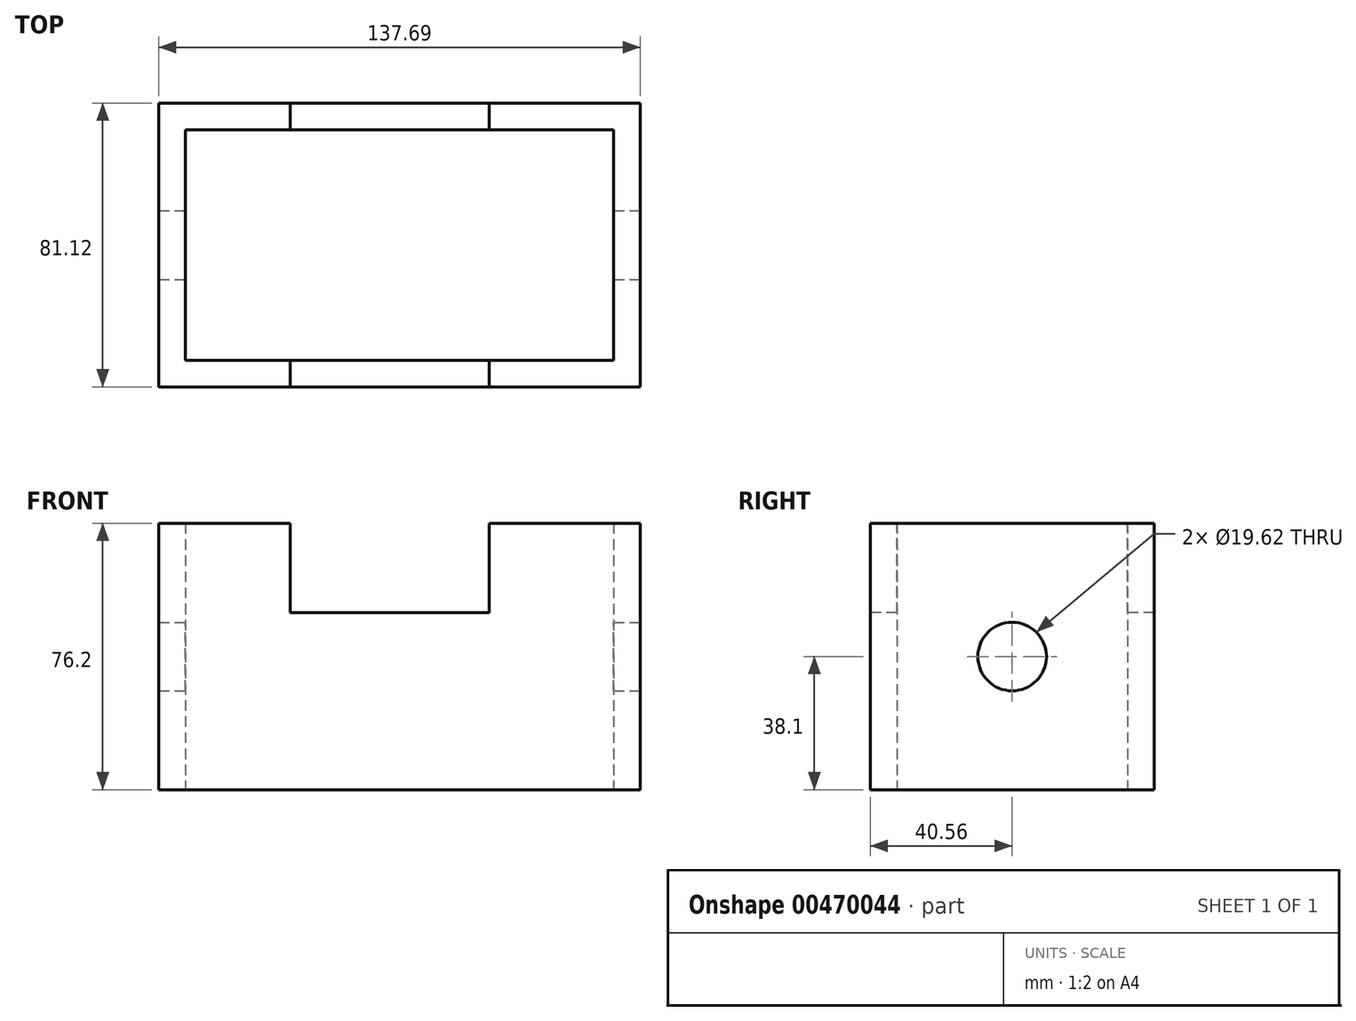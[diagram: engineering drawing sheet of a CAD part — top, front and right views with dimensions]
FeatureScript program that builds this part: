
annotation { "Feature Type Name" : "Feature", "Feature Type Description" : "" }
export const myFeature = defineFeature(function(context is Context, id is Id, definition is map)
    precondition{}
    {
        {
            var Q0;
            Q0=qCreatedBy(makeId("Top.planeOp"),FACE);
            var sketch = newSketch(context, id + "F0", { "sketchPlane" : qUnion([Q0])});
            skLineSegment(sketch, "E0.bottom", {"start": v(71.64, 40.56) * mm, "end": v(-66.05, 40.56) * mm});
            skLineSegment(sketch, "E0.top", {"start": v(71.64, -40.56) * mm, "end": v(-66.05, -40.56) * mm});
            skLineSegment(sketch, "E0.left", {"start": v(71.64, 40.56) * mm, "end": v(71.64, -40.56) * mm});
            skLineSegment(sketch, "E0.right", {"start": v(-66.05, 40.56) * mm, "end": v(-66.05, -40.56) * mm});
            skPoint(sketch, "E0.middle", {"position": v(2.8, 0) * mm});
            skSolve(sketch);
        }
        {
            var Q0;
            Q0=makeQuery(id+"F0.imprint","IMPRINT",FACE,{"disambiguationData":[TD([[makeQuery(id+"F0.imprint","IMPRINT",EDGE,{"derivedFrom":sQuery(id+"F0.wireOp",EDGE,"E0.bottom")}),1.0]])]});
            extrude(context, id + "F1", {"entities" : qUnion([Q0]), "depth" : 76.2 * mm});
        }
        {
            var Q0;
            Q0=makeQuery(id+"F1.opExtrude","CAP_FACE",FACE,{"disambiguationData":[OSD([sQuery(id+"F0.wireOp",EDGE,"E0.bottom"),sQuery(id+"F0.wireOp",EDGE,"E0.top"),sQuery(id+"F0.wireOp",EDGE,"E0.left"),sQuery(id+"F0.wireOp",EDGE,"E0.right")])],"isStart":false});
            var Q1;
            Q1=makeQuery(id+"F1.opExtrude","CAP_FACE",FACE,{"disambiguationData":[OSD([sQuery(id+"F0.wireOp",EDGE,"E0.bottom"),sQuery(id+"F0.wireOp",EDGE,"E0.top"),sQuery(id+"F0.wireOp",EDGE,"E0.left"),sQuery(id+"F0.wireOp",EDGE,"E0.right")])],"isStart":true});
            shell(context, id + "F2", {"entities" : qUnion([Q0, Q1]), "thickness" : 7.62 * mm});
        }
        {
            var Q0;
            Q0=makeQuery(id+"F1.opExtrude","SWEPT_FACE",FACE,{"disambiguationData":[OSD([sQuery(id+"F0.wireOp",EDGE,"E0.top")])]});
            var sketch = newSketch(context, id + "F3", { "sketchPlane" : qUnion([Q0])});
            skLineSegment(sketch, "E1.bottom", {"start": v(28.47, 50.61) * mm, "end": v(-28.47, 50.61) * mm});
            skLineSegment(sketch, "E1.top", {"start": v(28.47, 101.79) * mm, "end": v(-28.47, 101.79) * mm});
            skLineSegment(sketch, "E1.left", {"start": v(28.47, 50.61) * mm, "end": v(28.47, 101.79) * mm});
            skLineSegment(sketch, "E1.right", {"start": v(-28.47, 50.61) * mm, "end": v(-28.47, 101.79) * mm});
            skPoint(sketch, "E1.middle", {"position": v(0, 76.2) * mm});
            skSolve(sketch);
        }
        {
            var Q0;
            Q0 = qSketchRegion(id + "F3", true);
            extrude(context, id + "F4", {"entities" : qUnion([Q0]), "operationType" : NewBodyOperationType.REMOVE, "endBound" : BoundingType.THROUGH_ALL, "oppositeDirection" : true, "depth" : 25.4 * mm});
        }
        {
            var Q0;
            Q0=makeQuery(id+"F1.opExtrude","SWEPT_FACE",FACE,{"disambiguationData":[OSD([sQuery(id+"F0.wireOp",EDGE,"E0.left")])]});
            var sketch = newSketch(context, id + "F5", { "sketchPlane" : qUnion([Q0])});
            skLineSegment(sketch, "E2", {"start": v(0, 0) * mm, "end": v(0, 76.2) * mm, "construction": true});
            skCircle(sketch, "E3", {"center": v(0, 38.1) * mm, "radius": 9.81 * mm});
            skSolve(sketch);
        }
        {
            var Q0;
            Q0=makeQuery(id+"F5.imprint","IMPRINT",FACE,{"disambiguationData":[TD([[makeQuery(id+"F5.imprint","IMPRINT",EDGE,{"derivedFrom":sQuery(id+"F5.wireOp",EDGE,"E3")}),1.0]])]});
            extrude(context, id + "F6", {"entities" : qUnion([Q0]), "operationType" : NewBodyOperationType.REMOVE, "endBound" : BoundingType.THROUGH_ALL, "oppositeDirection" : true, "depth" : 25.4 * mm});
        }
    });
